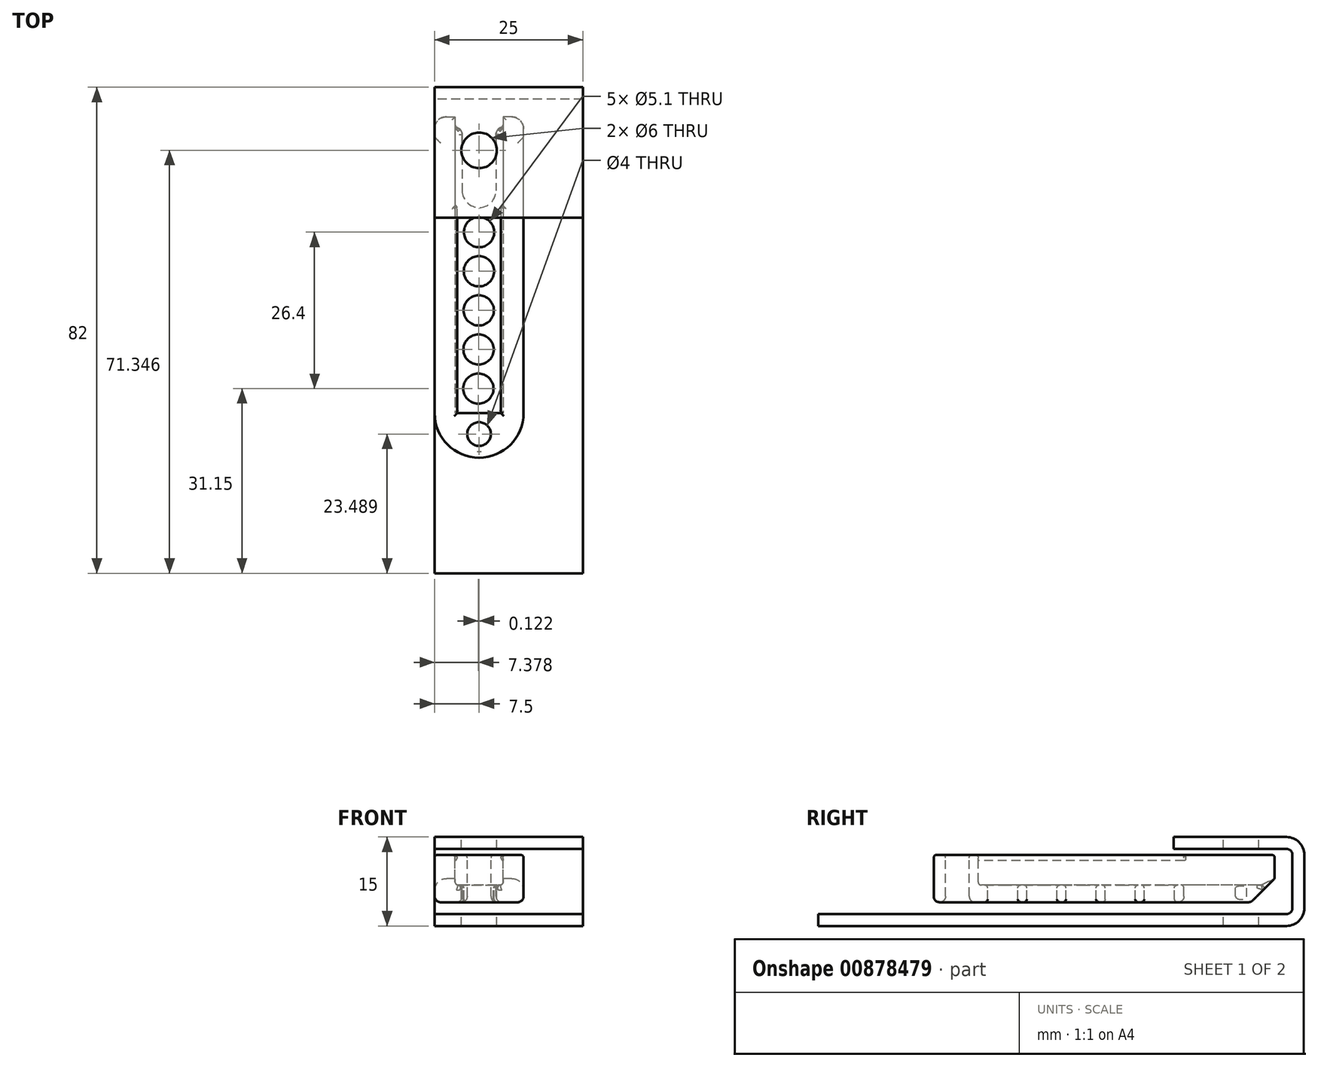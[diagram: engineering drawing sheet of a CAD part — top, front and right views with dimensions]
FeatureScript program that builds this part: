
annotation { "Feature Type Name" : "Feature", "Feature Type Description" : "" }
export const myFeature = defineFeature(function(context is Context, id is Id, definition is map)
    precondition{}
    {
        {
            var Q0;
            Q0=qCreatedBy(makeId("Top.planeOp"),FACE);
            var sketch = newSketch(context, id + "F0", { "sketchPlane" : qUnion([Q0])});
            skLineSegment(sketch, "E0.bottom", {"start": v(-7.5, -25) * mm, "end": v(7.5, -25) * mm});
            skLineSegment(sketch, "E0.top", {"start": v(-7.5, 25) * mm, "end": v(7.5, 25) * mm});
            skLineSegment(sketch, "E0.left", {"start": v(-7.5, -25) * mm, "end": v(-7.5, 25) * mm});
            skLineSegment(sketch, "E0.right", {"start": v(7.5, -25) * mm, "end": v(7.5, 25) * mm});
            skPoint(sketch, "E0.middle", {"position": v(0, 0) * mm});
            skCircle(sketch, "E1", {"center": v(0, -25) * mm, "radius": 7.5 * mm});
            skPoint(sketch, "E2.visualSharp", {"position": v(-7.5, 25) * mm});
            skPoint(sketch, "E3.visualSharp", {"position": v(7.5, 25) * mm});
            skSolve(sketch);
        }
        {
            var Q0;
            Q0 = qSketchRegion(id + "F0", true);
            extrude(context, id + "F1", {"entities" : qUnion([Q0]), "depth" : 8 * mm, "offsetDistance" : 25 * mm});
        }
        {
            var Q0;
            Q0=makeQuery(id+"F1.opExtrude","CAP_FACE",FACE,{"disambiguationData":[OSD([sQuery(id+"F0.wireOp",EDGE,"E0.top"),sQuery(id+"F0.wireOp",EDGE,"E0.left"),sQuery(id+"F0.wireOp",EDGE,"E0.right"),sQuery(id+"F0.wireOp",EDGE,"E1")])],"isStart":false});
            var sketch = newSketch(context, id + "F2", { "sketchPlane" : qUnion([Q0])});
            skLineSegment(sketch, "E4.bottom", {"start": v(-4.05, 25) * mm, "end": v(4.05, 25) * mm});
            skLineSegment(sketch, "E4.top", {"start": v(-4.05, -25) * mm, "end": v(4.05, -25) * mm});
            skLineSegment(sketch, "E4.left", {"start": v(-4.05, 25) * mm, "end": v(-4.05, -25) * mm});
            skLineSegment(sketch, "E4.right", {"start": v(4.05, 25) * mm, "end": v(4.05, -25) * mm});
            skPoint(sketch, "E4.middle", {"position": v(0, 0) * mm});
            skCircle(sketch, "E5", {"center": v(0, -28.51) * mm, "radius": 2 * mm});
            skSolve(sketch);
        }
        {
            var Q0;
            Q0 = qSketchRegion(id + "F2", true);
            extrude(context, id + "F3", {"entities" : qUnion([Q0]), "operationType" : NewBodyOperationType.REMOVE, "oppositeDirection" : true, "depth" : 5.1 * mm, "offsetDistance" : 25 * mm});
        }
        {
            var Q0;
            Q0=makeQuery(id+"F1.opExtrude","CAP_FACE",FACE,{"disambiguationData":[OSD([sQuery(id+"F0.wireOp",EDGE,"E0.top"),sQuery(id+"F0.wireOp",EDGE,"E0.left"),sQuery(id+"F0.wireOp",EDGE,"E0.right"),sQuery(id+"F0.wireOp",EDGE,"E1")])],"isStart":false});
            var sketch = newSketch(context, id + "F4", { "sketchPlane" : qUnion([Q0])});
            skCircle(sketch, "E6", {"center": v(0, -28.51) * mm, "radius": 2 * mm});
            skSolve(sketch);
        }
        {
            var Q0;
            Q0 = qSketchRegion(id + "F4", true);
            extrude(context, id + "F5", {"entities" : qUnion([Q0]), "operationType" : NewBodyOperationType.REMOVE, "oppositeDirection" : true, "depth" : 25 * mm, "offsetDistance" : 25 * mm});
        }
        {
            var Q0;
            Q0=makeQuery(id+"F1.opExtrude","CAP_EDGE",EDGE,{"disambiguationData":[OSD([sQuery(id+"F0.wireOp",EDGE,"E0.top")])],"isStart":true});
            chamfer(context, id + "F6", {"entities" : qUnion([Q0]), "width" : 4 * mm, "tangentPropagation" : true});
        }
        {
            var Q0;
            Q0=makeQuery(id+"F1.opExtrude","SWEPT_EDGE",EDGE,{"disambiguationData":[OSD([sQuery(id+"F0.wireOp",EDGE,"E0.top"),sQuery(id+"F0.wireOp",EDGE,"E0.right")])]});
            var Q1;
            Q1=makeQuery(id+"F1.opExtrude","SWEPT_EDGE",EDGE,{"disambiguationData":[OSD([sQuery(id+"F0.wireOp",EDGE,"E0.top"),sQuery(id+"F0.wireOp",EDGE,"E0.left")])]});
            fillet(context, id + "F7", {"entities" : qUnion([Q0, Q1]), "radius" : 2 * mm, "tangentPropagation" : true, "allowEdgeOverflow" : false});
        }
        {
            var Q0;
            Q0=makeQuery(id+"F3.boolean.opBoolean","COPY",FACE,{"derivedFrom":makeQuery(id+"F3.opExtrude","CAP_FACE",FACE,{"disambiguationData":[OSD([sQuery(id+"F2.wireOp",EDGE,"E4.bottom"),sQuery(id+"F2.wireOp",EDGE,"E4.top"),sQuery(id+"F2.wireOp",EDGE,"E4.left"),sQuery(id+"F2.wireOp",EDGE,"E4.right")])],"isStart":false})});
            var sketch = newSketch(context, id + "F8", { "sketchPlane" : qUnion([Q0])});
            skLineSegment(sketch, "E7.left", {"start": v(-2.85, 24.64) * mm, "end": v(-2.85, 12.55) * mm});
            skLineSegment(sketch, "E7.right", {"start": v(2.85, 24.64) * mm, "end": v(2.85, 12.55) * mm});
            skArc(sketch, "E8", {"start": v(-2.85, 12.55) * mm, "mid": v(0, 9.7) * mm, "end": v(2.85, 12.55) * mm});
            skLineSegment(sketch, "E9", {"start": v(-2.85, 24.64) * mm, "end": v(2.85, 24.64) * mm});
            skSolve(sketch);
        }
        {
            var Q0;
            Q0 = qSketchRegion(id + "F8", true);
            extrude(context, id + "F9", {"entities" : qUnion([Q0]), "operationType" : NewBodyOperationType.REMOVE, "oppositeDirection" : true, "depth" : 25 * mm, "offsetDistance" : 25 * mm});
        }
        {
            var Q0;
            Q0=makeQuery(id+"F1.opExtrude","CAP_FACE",FACE,{"disambiguationData":[OSD([sQuery(id+"F0.wireOp",EDGE,"E0.top"),sQuery(id+"F0.wireOp",EDGE,"E0.left"),sQuery(id+"F0.wireOp",EDGE,"E0.right"),sQuery(id+"F0.wireOp",EDGE,"E1")])],"isStart":true});
            var Q1;
            Q1=makeQuery(id+"F9.boolean.opBoolean","INTERSECT",EDGE,{"derivedFrom":[makeQuery(id+"F6.opChamfer","BLEND_FACE",FACE,{"disambiguationData":[OSD([sQuery(id+"F0.wireOp",EDGE,"E0.top")])]}),makeQuery(id+"F9.opExtrude","SWEPT_FACE",FACE,{"disambiguationData":[OSD([sQuery(id+"F8.wireOp",EDGE,"E7.left")])]})]});
            var Q2;
            Q2=makeQuery(id+"F9.boolean.opBoolean","INTERSECT",EDGE,{"derivedFrom":[makeQuery(id+"F6.opChamfer","BLEND_FACE",FACE,{"disambiguationData":[OSD([sQuery(id+"F0.wireOp",EDGE,"E0.top")])]}),makeQuery(id+"F9.opExtrude","SWEPT_FACE",FACE,{"disambiguationData":[OSD([sQuery(id+"F8.wireOp",EDGE,"E7.right")])]})]});
            fillet(context, id + "F10", {"entities" : qUnion([Q0, Q1, Q2]), "radius" : 1 * mm, "tangentPropagation" : true, "allowEdgeOverflow" : false});
        }
        {
            var Q0;
            Q0=makeQuery(id+"F3.boolean.opBoolean","COPY",FACE,{"derivedFrom":makeQuery(id+"F3.opExtrude","SWEPT_FACE",FACE,{"disambiguationData":[OSD([sQuery(id+"F2.wireOp",EDGE,"E4.top")])]})});
            var sketch = newSketch(context, id + "F11", { "sketchPlane" : qUnion([Q0])});
            skLineSegment(sketch, "E10", {"start": v(-4.05, 8) * mm, "end": v(-2.55, 8) * mm});
            skLineSegment(sketch, "E11", {"start": v(-2.55, 8) * mm, "end": v(-4.05, 7) * mm});
            skLineSegment(sketch, "E12", {"start": v(-4.05, 7) * mm, "end": v(-4.05, 8) * mm});
            skLineSegment(sketch, "E13.MirrorCS", {"start": v(4.05, 7) * mm, "end": v(4.05, 8) * mm});
            skLineSegment(sketch, "E14.MirrorCS", {"start": v(2.55, 8) * mm, "end": v(4.05, 7) * mm});
            skLineSegment(sketch, "E15.MirrorCS", {"start": v(4.05, 8) * mm, "end": v(2.55, 8) * mm});
            skSolve(sketch);
        }
        {
            var Q0;
            Q0 = qSketchRegion(id + "F11", true);
            extrude(context, id + "F12", {"entities" : qUnion([Q0]), "operationType" : NewBodyOperationType.ADD, "depth" : 35 * mm, "offsetDistance" : 25 * mm});
        }
        {
            var Q0;
            Q0=makeQuery(id+"F3.boolean.opBoolean","COPY",FACE,{"derivedFrom":makeQuery(id+"F3.opExtrude","CAP_FACE",FACE,{"disambiguationData":[OSD([sQuery(id+"F2.wireOp",EDGE,"E4.bottom"),sQuery(id+"F2.wireOp",EDGE,"E4.top"),sQuery(id+"F2.wireOp",EDGE,"E4.left"),sQuery(id+"F2.wireOp",EDGE,"E4.right")])],"isStart":false})});
            var sketch = newSketch(context, id + "F13", { "sketchPlane" : qUnion([Q0])});
            skCircle(sketch, "E16", {"center": v(0, 5.55) * mm, "radius": 2.55 * mm});
            skCircle(sketch, "E17.1.0.0", {"center": v(-0.03, -1.05) * mm, "radius": 2.55 * mm});
            skCircle(sketch, "E17.2.0.0", {"center": v(-0.06, -7.65) * mm, "radius": 2.55 * mm});
            skCircle(sketch, "E17.3.0.0", {"center": v(-0.1, -14.25) * mm, "radius": 2.55 * mm});
            skCircle(sketch, "E17.4.0.0", {"center": v(-0.12, -20.85) * mm, "radius": 2.55 * mm});
            skLineSegment(sketch, "E17.direction1", {"start": v(0, 5.55) * mm, "end": v(-0.03, -1.05) * mm, "construction": true});
            skSolve(sketch);
        }
        {
            var Q0;
            Q0 = qSketchRegion(id + "F13", true);
            extrude(context, id + "F14", {"entities" : qUnion([Q0]), "operationType" : NewBodyOperationType.REMOVE, "oppositeDirection" : true, "depth" : 25 * mm, "offsetDistance" : 25 * mm});
        }
        {
            var Q0;
            Q0=makeQuery(id+"F12.boolean.opBoolean","MERGE",FACE,{"derivedFrom":[makeQuery(id+"F1.opExtrude","CAP_FACE",FACE,{"disambiguationData":[OSD([sQuery(id+"F0.wireOp",EDGE,"E0.top"),sQuery(id+"F0.wireOp",EDGE,"E0.left"),sQuery(id+"F0.wireOp",EDGE,"E0.right"),sQuery(id+"F0.wireOp",EDGE,"E1")])],"isStart":false}),makeQuery(id+"F12.opExtrude","SWEPT_FACE",FACE,{"disambiguationData":[OSD([sQuery(id+"F11.wireOp",EDGE,"E10")])]}),makeQuery(id+"F12.opExtrude","SWEPT_FACE",FACE,{"disambiguationData":[OSD([sQuery(id+"F11.wireOp",EDGE,"E15.MirrorCS")])]})]});
            var Q1;
            Q1=makeQuery(id+"F3.boolean.opBoolean","COPY",FACE,{"derivedFrom":makeQuery(id+"F3.opExtrude","CAP_FACE",FACE,{"disambiguationData":[OSD([sQuery(id+"F2.wireOp",EDGE,"E4.bottom"),sQuery(id+"F2.wireOp",EDGE,"E4.top"),sQuery(id+"F2.wireOp",EDGE,"E4.left"),sQuery(id+"F2.wireOp",EDGE,"E4.right")])],"isStart":false})});
            var Q2;
            Q2=makeQuery(id+"F3.boolean.opBoolean","COPY",EDGE,{"derivedFrom":makeQuery(id+"F3.opExtrude","SWEPT_EDGE",EDGE,{"disambiguationData":[OSD([sQuery(id+"F0.wireOp",EDGE,"E0.top"),sQuery(id+"F2.wireOp",EDGE,"E4.bottom"),sQuery(id+"F2.wireOp",EDGE,"E4.left")])]})});
            var Q3;
            Q3=makeQuery(id+"F3.boolean.opBoolean","COPY",EDGE,{"derivedFrom":makeQuery(id+"F3.opExtrude","SWEPT_EDGE",EDGE,{"disambiguationData":[OSD([sQuery(id+"F0.wireOp",EDGE,"E0.top"),sQuery(id+"F2.wireOp",EDGE,"E4.bottom"),sQuery(id+"F2.wireOp",EDGE,"E4.right")])]})});
            fillet(context, id + "F15", {"entities" : qUnion([Q0, Q1, Q2, Q3]), "radius" : 0.5 * mm, "tangentPropagation" : true, "allowEdgeOverflow" : false});
        }
        {
            var Q0;
            Q0=makeQuery(id+"F14.boolean.opBoolean","INTERSECT",EDGE,{"derivedFrom":[makeQuery(id+"F1.opExtrude","CAP_FACE",FACE,{"disambiguationData":[OSD([sQuery(id+"F0.wireOp",EDGE,"E0.top"),sQuery(id+"F0.wireOp",EDGE,"E0.left"),sQuery(id+"F0.wireOp",EDGE,"E0.right"),sQuery(id+"F0.wireOp",EDGE,"E1")])],"isStart":true}),makeQuery(id+"F14.opExtrude","SWEPT_FACE",FACE,{"disambiguationData":[OSD([sQuery(id+"F13.wireOp",EDGE,"E16")])]})]});
            var Q1;
            Q1=makeQuery(id+"F14.boolean.opBoolean","INTERSECT",EDGE,{"derivedFrom":[makeQuery(id+"F1.opExtrude","CAP_FACE",FACE,{"disambiguationData":[OSD([sQuery(id+"F0.wireOp",EDGE,"E0.top"),sQuery(id+"F0.wireOp",EDGE,"E0.left"),sQuery(id+"F0.wireOp",EDGE,"E0.right"),sQuery(id+"F0.wireOp",EDGE,"E1")])],"isStart":true}),makeQuery(id+"F14.opExtrude","SWEPT_FACE",FACE,{"disambiguationData":[OSD([sQuery(id+"F13.wireOp",EDGE,"E17.1.0.0")])]})]});
            var Q2;
            Q2=makeQuery(id+"F14.boolean.opBoolean","INTERSECT",EDGE,{"derivedFrom":[makeQuery(id+"F1.opExtrude","CAP_FACE",FACE,{"disambiguationData":[OSD([sQuery(id+"F0.wireOp",EDGE,"E0.top"),sQuery(id+"F0.wireOp",EDGE,"E0.left"),sQuery(id+"F0.wireOp",EDGE,"E0.right"),sQuery(id+"F0.wireOp",EDGE,"E1")])],"isStart":true}),makeQuery(id+"F14.opExtrude","SWEPT_FACE",FACE,{"disambiguationData":[OSD([sQuery(id+"F13.wireOp",EDGE,"E17.2.0.0")])]})]});
            var Q3;
            Q3=makeQuery(id+"F14.boolean.opBoolean","INTERSECT",EDGE,{"derivedFrom":[makeQuery(id+"F1.opExtrude","CAP_FACE",FACE,{"disambiguationData":[OSD([sQuery(id+"F0.wireOp",EDGE,"E0.top"),sQuery(id+"F0.wireOp",EDGE,"E0.left"),sQuery(id+"F0.wireOp",EDGE,"E0.right"),sQuery(id+"F0.wireOp",EDGE,"E1")])],"isStart":true}),makeQuery(id+"F14.opExtrude","SWEPT_FACE",FACE,{"disambiguationData":[OSD([sQuery(id+"F13.wireOp",EDGE,"E17.3.0.0")])]})]});
            var Q4;
            Q4=makeQuery(id+"F14.boolean.opBoolean","INTERSECT",EDGE,{"derivedFrom":[makeQuery(id+"F1.opExtrude","CAP_FACE",FACE,{"disambiguationData":[OSD([sQuery(id+"F0.wireOp",EDGE,"E0.top"),sQuery(id+"F0.wireOp",EDGE,"E0.left"),sQuery(id+"F0.wireOp",EDGE,"E0.right"),sQuery(id+"F0.wireOp",EDGE,"E1")])],"isStart":true}),makeQuery(id+"F14.opExtrude","SWEPT_FACE",FACE,{"disambiguationData":[OSD([sQuery(id+"F13.wireOp",EDGE,"E17.4.0.0")])]})]});
            fillet(context, id + "F16", {"entities" : qUnion([Q0, Q1, Q2, Q3, Q4]), "radius" : 0.5 * mm, "tangentPropagation" : true, "allowEdgeOverflow" : false});
        }
        {
            var Q0;
            {var subQ0=sQuery(id+"F11.wireOp",EDGE,"E15.MirrorCS");Q0=makeQuery(id+"F15.opFillet","BLEND_EDGE",EDGE,{"blendedFrom":[makeQuery(id+"F12.opExtrude","SWEPT_EDGE",EDGE,{"disambiguationData":[OSD([sQuery(id+"F2.wireOp",EDGE,"E4.top"),sQuery(id+"F11.wireOp",EDGE,"E14.MirrorCS"),subQ0])]}),makeQuery(id+"F12.opExtrude","CAP_EDGE",EDGE,{"disambiguationData":[OSD([subQ0])],"isStart":false})],"blendedInto":[]});}
            var Q1;
            {var subQ0=sQuery(id+"F11.wireOp",EDGE,"E10");Q1=makeQuery(id+"F15.opFillet","BLEND_EDGE",EDGE,{"blendedFrom":[makeQuery(id+"F12.opExtrude","SWEPT_EDGE",EDGE,{"disambiguationData":[OSD([sQuery(id+"F2.wireOp",EDGE,"E4.top"),subQ0,sQuery(id+"F11.wireOp",EDGE,"E11")])]}),makeQuery(id+"F12.opExtrude","CAP_EDGE",EDGE,{"disambiguationData":[OSD([subQ0])],"isStart":false})],"blendedInto":[]});}
            fillet(context, id + "F17", {"entities" : qUnion([Q0, Q1]), "radius" : 0.3 * mm, "tangentPropagation" : true, "allowEdgeOverflow" : false});
        }
        {
            var Q0;
            Q0=makeQuery(id+"F1.opExtrude","SWEPT_FACE",FACE,{"disambiguationData":[OSD([sQuery(id+"F0.wireOp",EDGE,"E0.left")])]});
            var sketch = newSketch(context, id + "F18", { "sketchPlane" : qUnion([Q0])});
            skLineSegment(sketch, "E18", {"start": v(-8, 9) * mm, "end": v(-27, 9) * mm});
            skLineSegment(sketch, "E19", {"start": v(-28, 8) * mm, "end": v(-28, -1) * mm});
            skLineSegment(sketch, "E20", {"start": v(-27, -2) * mm, "end": v(52, -2) * mm});
            skLineSegment(sketch, "E21.0", {"start": v(-8, 11) * mm, "end": v(-27, 11) * mm});
            skLineSegment(sketch, "E22.0", {"start": v(-30, 8) * mm, "end": v(-30, -1) * mm});
            skLineSegment(sketch, "E23.0", {"start": v(-27, -4) * mm, "end": v(52, -4) * mm});
            skArc(sketch, "E24.filletArc", {"start": v(-27, 11) * mm, "mid": v(-29.12, 10.12) * mm, "end": v(-30, 8) * mm});
            skPoint(sketch, "E25.visualSharp", {"position": v(-28, 9) * mm});
            skArc(sketch, "E25.filletArc", {"start": v(-27, 9) * mm, "mid": v(-27.7, 8.7) * mm, "end": v(-28, 8) * mm});
            skPoint(sketch, "E26.visualSharp", {"position": v(-28, -2) * mm});
            skArc(sketch, "E26.filletArc", {"start": v(-28, -1) * mm, "mid": v(-27.7, -1.7) * mm, "end": v(-27, -2) * mm});
            skArc(sketch, "E27.filletArc", {"start": v(-30, -1) * mm, "mid": v(-29.12, -3.12) * mm, "end": v(-27, -4) * mm});
            skLineSegment(sketch, "E28", {"start": v(-8, 9) * mm, "end": v(-8, 11) * mm});
            skLineSegment(sketch, "E29", {"start": v(52, -4) * mm, "end": v(52, -2) * mm});
            skSolve(sketch);
        }
        {
            var Q0;
            Q0 = qSketchRegion(id + "F18", true);
            extrude(context, id + "F19", {"entities" : qUnion([Q0]), "oppositeDirection" : true, "depth" : 25 * mm, "offsetDistance" : 25 * mm});
        }
        {
            var Q0;
            Q0=makeQuery(id+"F19.opExtrude","SWEPT_FACE",FACE,{"disambiguationData":[OSD([sQuery(id+"F18.wireOp",EDGE,"E21.0")])]});
            var sketch = newSketch(context, id + "F20", { "sketchPlane" : qUnion([Q0])});
            skCircle(sketch, "E30", {"center": v(0, 19.35) * mm, "radius": 3 * mm});
            skSolve(sketch);
        }
        {
            var Q0;
            Q0 = qSketchRegion(id + "F20", true);
            extrude(context, id + "F21", {"entities" : qUnion([Q0]), "operationType" : NewBodyOperationType.REMOVE, "oppositeDirection" : true, "depth" : 25 * mm, "offsetDistance" : 25 * mm});
        }
    });
